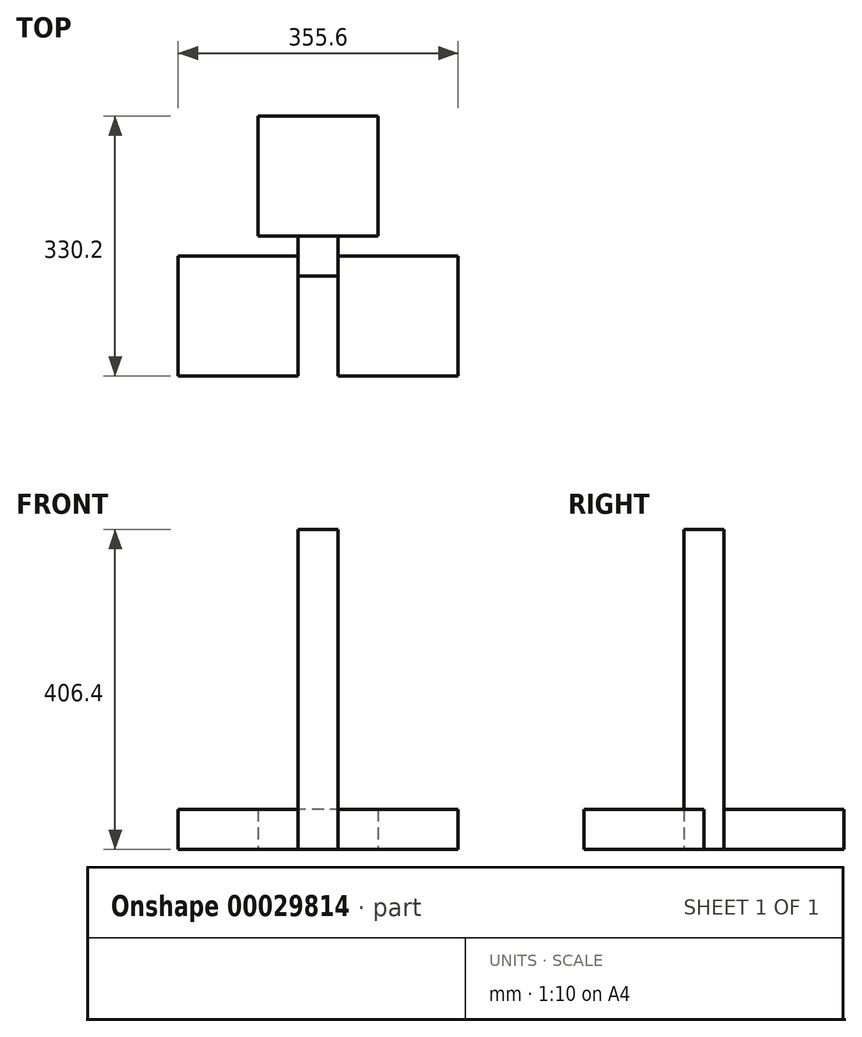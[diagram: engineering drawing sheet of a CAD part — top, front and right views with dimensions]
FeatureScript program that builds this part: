
annotation { "Feature Type Name" : "Feature", "Feature Type Description" : "" }
export const myFeature = defineFeature(function(context is Context, id is Id, definition is map)
    precondition{}
    {
        {
            var Q0;
            Q0=qCreatedBy(makeId("Top.planeOp"),FACE);
            var sketch = newSketch(context, id + "F0", { "sketchPlane" : qUnion([Q0])});
            skLineSegment(sketch, "E0.rect.bottom", {"start": v(25.4, 25.4) * mm, "end": v(-25.4, 25.4) * mm});
            skLineSegment(sketch, "E0.rect.top", {"start": v(25.4, -25.4) * mm, "end": v(-25.4, -25.4) * mm});
            skLineSegment(sketch, "E0.rect.left", {"start": v(25.4, 25.4) * mm, "end": v(25.4, -25.4) * mm});
            skLineSegment(sketch, "E0.rect.right", {"start": v(-25.4, 25.4) * mm, "end": v(-25.4, -25.4) * mm});
            skPoint(sketch, "E0.rect.middle", {"position": v(0, 0) * mm});
            skLineSegment(sketch, "E1.bottom", {"start": v(-25.4, 0) * mm, "end": v(-177.8, 0) * mm});
            skLineSegment(sketch, "E1.top", {"start": v(-25.4, -152.4) * mm, "end": v(-177.8, -152.4) * mm});
            skLineSegment(sketch, "E1.left", {"start": v(-25.4, 0) * mm, "end": v(-25.4, -152.4) * mm});
            skLineSegment(sketch, "E1.right", {"start": v(-177.8, 0) * mm, "end": v(-177.8, -152.4) * mm});
            skLineSegment(sketch, "E2.bottom", {"start": v(25.4, 0) * mm, "end": v(177.8, 0) * mm});
            skLineSegment(sketch, "E2.top", {"start": v(25.4, -152.4) * mm, "end": v(177.8, -152.4) * mm});
            skLineSegment(sketch, "E2.left", {"start": v(25.4, 0) * mm, "end": v(25.4, -152.4) * mm});
            skLineSegment(sketch, "E2.right", {"start": v(177.8, 0) * mm, "end": v(177.8, -152.4) * mm});
            skLineSegment(sketch, "E3.bottom", {"start": v(0, 25.4) * mm, "end": v(76.2, 25.4) * mm});
            skLineSegment(sketch, "E3.right", {"start": v(76.2, 25.4) * mm, "end": v(76.2, 177.8) * mm});
            skLineSegment(sketch, "E4.bottom", {"start": v(0, 25.4) * mm, "end": v(-76.2, 25.4) * mm});
            skLineSegment(sketch, "E4.right", {"start": v(-76.2, 25.4) * mm, "end": v(-76.2, 177.8) * mm});
            skLineSegment(sketch, "E5", {"start": v(-76.2, 177.8) * mm, "end": v(76.2, 177.8) * mm});
            skSolve(sketch);
        }
        {
            var Q0;
            {var subQ3=sQuery(id+"F0.wireOp",EDGE,"E1.bottom");Q0=makeQuery(id+"F0.imprint","IMPRINT",FACE,{"disambiguationData":[TD([[makeQuery(id+"F0.imprint","IMPRINT",EDGE,{"derivedFrom":subQ3}),1.0]])]});}
            var Q1;
            {var subQ3=sQuery(id+"F0.wireOp",EDGE,"E2.bottom");Q1=makeQuery(id+"F0.imprint","IMPRINT",FACE,{"disambiguationData":[TD([[makeQuery(id+"F0.imprint","IMPRINT",EDGE,{"derivedFrom":subQ3}),-1.0]])]});}
            var Q2;
            {var subQ5=sQuery(id+"F0.wireOp",EDGE,"E3.right");Q2=makeQuery(id+"F0.imprint","IMPRINT",FACE,{"disambiguationData":[TD([[makeQuery(id+"F0.imprint","IMPRINT",EDGE,{"derivedFrom":subQ5}),1.0]])]});}
            extrude(context, id + "F1", {"entities" : qUnion([Q0, Q1, Q2]), "depth" : 50.8 * mm});
        }
        {
            var Q0;
            {var subQ6=sQuery(id+"F0.wireOp",EDGE,"E0.rect.top");Q0=makeQuery(id+"F0.imprint","IMPRINT",FACE,{"disambiguationData":[TD([[makeQuery(id+"F0.imprint","IMPRINT",EDGE,{"derivedFrom":subQ6}),-1.0]])]});}
            extrude(context, id + "F2", {"entities" : qUnion([Q0]), "depth" : 406.4 * mm});
        }
    });
